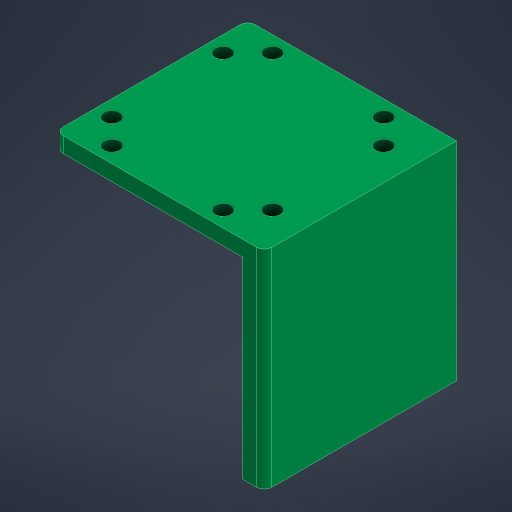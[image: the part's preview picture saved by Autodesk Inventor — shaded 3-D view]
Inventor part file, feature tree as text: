
AUTODESK INVENTOR PART (.ipt)
format: ipt  version: 2023.4 (Build 274418000, 418)  size: 218,624 bytes
history: native  units: mm
features: extrude x5, other x4, sketch x3, reference x2, plane x1, fillet x1, projected_geometry x1
ambient origin geometry x8: Origin, YZ Plane, XZ Plane, XY Plane, X Axis, Y Axis, Z Axis, Center Point
bodies: Solid1 (feature_tree)
feature tree (17):
  sketch  "Sketch1"  dims[d0=4.0mm d1=0.0mm d3=6.25mm]
  plane  "Work Plane1"
  extrude  "Extrusion1"  Depth=4.0mm
  sketch  "Sketch2"  dims[d4=4.125mm d5=2.0mm d6=0.0mm]
  extrude  "Extrusion2"  Depth=2.0mm TaperAngle=0.0deg
  extrude  "Extrusion3"  Depth=49.8mm TaperAngle=0.0deg
  extrude  "Extrusion4"  Depth=2.0mm
  fillet  "Fillet1"  Radius=5.0mm
  extrude  "Extrusion5"  Depth=49.8mm TaperAngle=0.0deg
  reference  "Reference1"
  projected_geometry  "Projected Loop1"
  sketch  "Sketch3"  dims[d7=2.0mm d8=0.0mm d9=49.8mm d10=0.0mm d11=2.0mm d12=5.0mm d13=49.8mm d14=0.0mm d15=0.125mm]
  reference  "Reference2"
  other  "<path>\Projects\Project Protocube\Protocube\CAD, STL, OBJ Files\1 CAD\Cube 1x1 V5.iam"
  other  "Cube 1x1 V5.iam"
  other  "Cube 1x1 Top V5 Closed Slotted:1"
  other  "Cube 1x1 Bottom V5 Closed Slotted:1"
note: 1 file-system path scrubbed to <path> (originals preserved in map.json)
